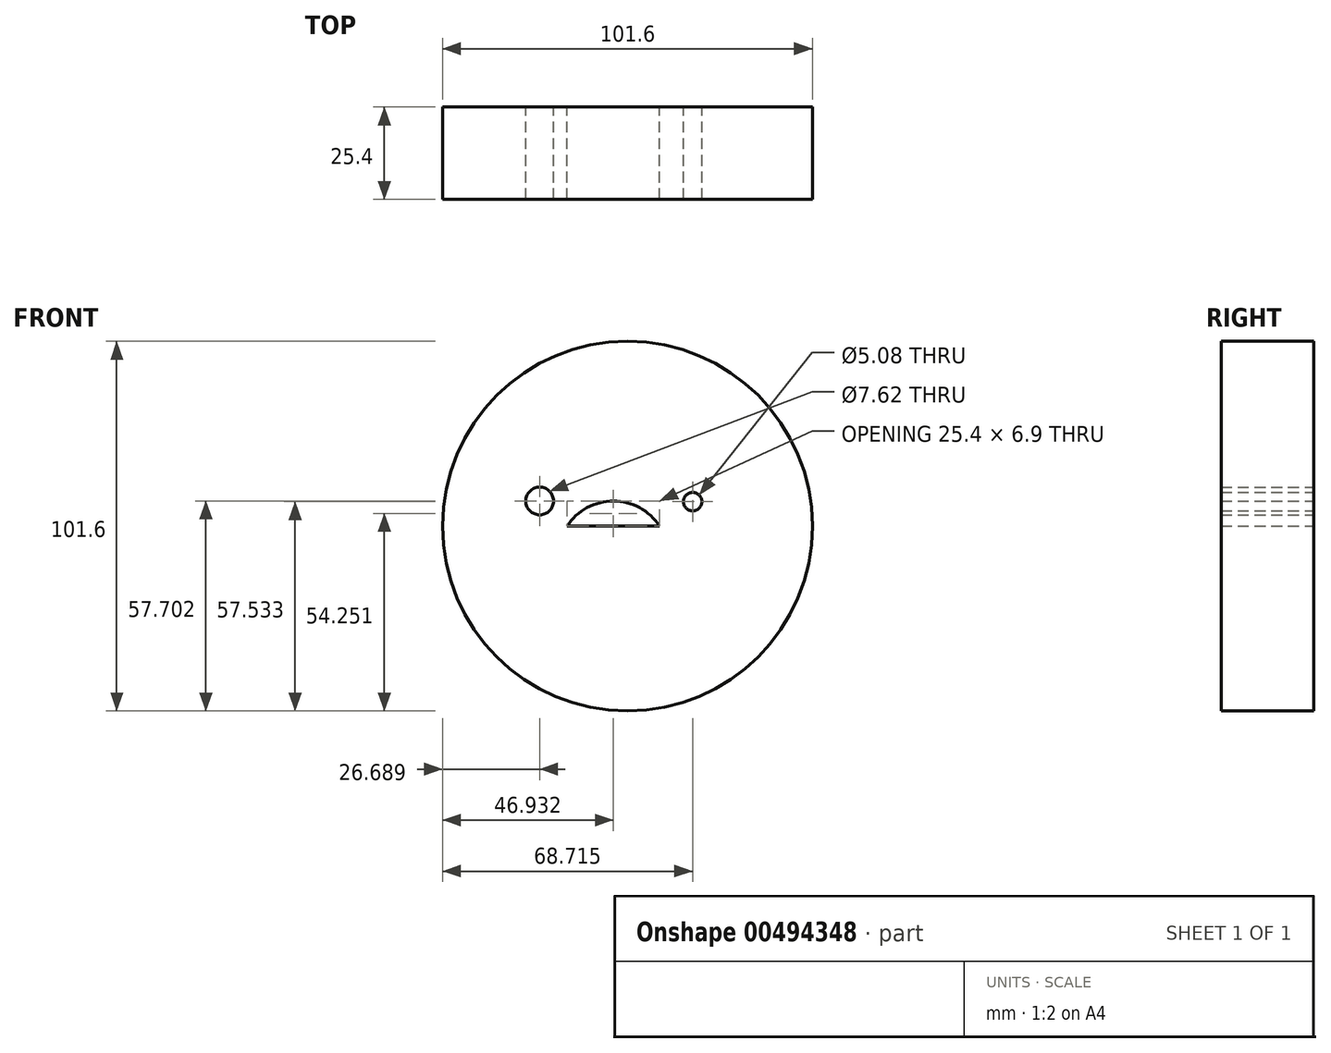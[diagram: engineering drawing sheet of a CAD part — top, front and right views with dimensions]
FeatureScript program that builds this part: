
annotation { "Feature Type Name" : "Feature", "Feature Type Description" : "" }
export const myFeature = defineFeature(function(context is Context, id is Id, definition is map)
    precondition{}
    {
        {
            var Q0;
            Q0=qCreatedBy(makeId("Front.planeOp"),FACE);
            var sketch = newSketch(context, id + "F0", { "sketchPlane" : qUnion([Q0])});
            skCircle(sketch, "E0", {"center": v(0, 0) * mm, "radius": 50.8 * mm});
            skLineSegment(sketch, "E1", {"start": v(-16.57, 0) * mm, "end": v(8.83, 0) * mm});
            skArc(sketch, "E2", {"start": v(8.83, 0) * mm, "mid": v(-3.87, 6.9) * mm, "end": v(-16.57, 0) * mm});
            skCircle(sketch, "E3", {"center": v(17.91, 6.73) * mm, "radius": 2.54 * mm});
            skCircle(sketch, "E4", {"center": v(-24.11, 6.9) * mm, "radius": 3.81 * mm});
            skPoint(sketch, "E4.centerSnap0", {"position": v(-3.87, 6.9) * mm});
            skSolve(sketch);
        }
        {
            var Q0;
            Q0=makeQuery(id+"F0.imprint","IMPRINT",FACE,{"disambiguationData":[TD([[makeQuery(id+"F0.imprint","IMPRINT",EDGE,{"derivedFrom":sQuery(id+"F0.wireOp",EDGE,"E0")}),1.0]])]});
            extrude(context, id + "F1", {"entities" : qUnion([Q0]), "depth" : 25.4 * mm});
        }
    });
